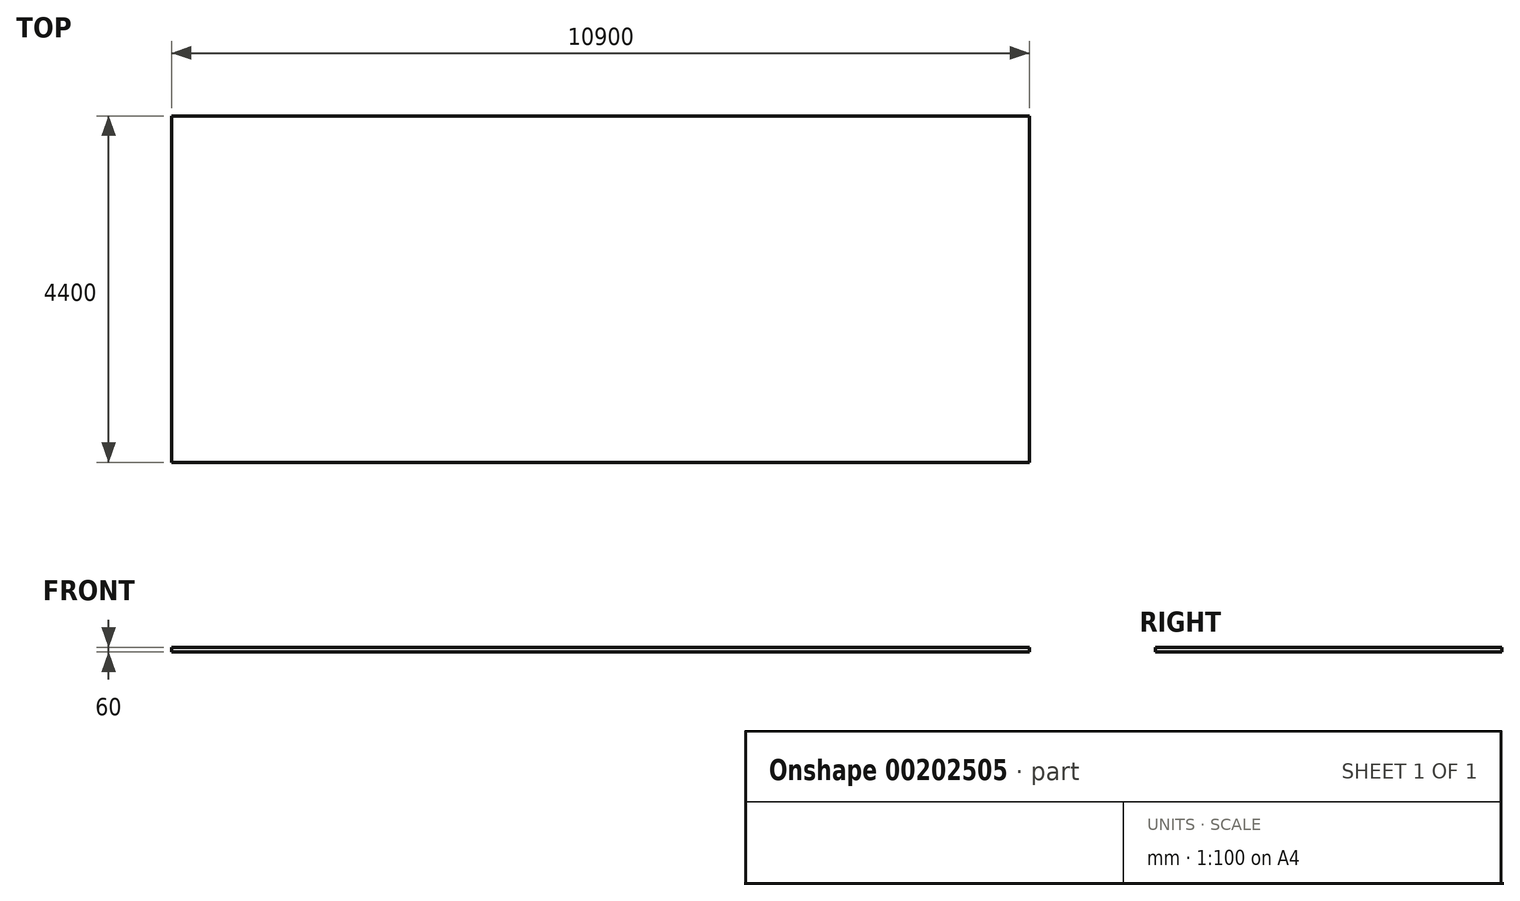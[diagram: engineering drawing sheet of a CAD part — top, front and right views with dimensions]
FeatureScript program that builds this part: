
annotation { "Feature Type Name" : "Feature", "Feature Type Description" : "" }
export const myFeature = defineFeature(function(context is Context, id is Id, definition is map)
    precondition{}
    {
        {
            var Q0;
            Q0=qCreatedBy(makeId("Top.planeOp"),FACE);
            var sketch = newSketch(context, id + "F0", { "sketchPlane" : qUnion([Q0])});
            skLineSegment(sketch, "E0.bottom", {"start": v(-5458.44, 1714.36) * mm, "end": v(5441.56, 1714.36) * mm});
            skLineSegment(sketch, "E0.top", {"start": v(-5458.44, -2685.64) * mm, "end": v(5441.56, -2685.64) * mm});
            skLineSegment(sketch, "E0.left", {"start": v(-5458.44, 1714.36) * mm, "end": v(-5458.44, -2685.64) * mm});
            skLineSegment(sketch, "E0.right", {"start": v(5441.56, 1714.36) * mm, "end": v(5441.56, -2685.64) * mm});
            skSolve(sketch);
        }
        {
            var Q0;
            Q0=makeQuery(id+"F0.imprint","IMPRINT",FACE,{"disambiguationData":[TD([[makeQuery(id+"F0.imprint","IMPRINT",EDGE,{"derivedFrom":sQuery(id+"F0.wireOp",EDGE,"E0.bottom")}),-1.0]])]});
            extrude(context, id + "F1", {"entities" : qUnion([Q0]), "depth" : 60 * mm});
        }
    });
